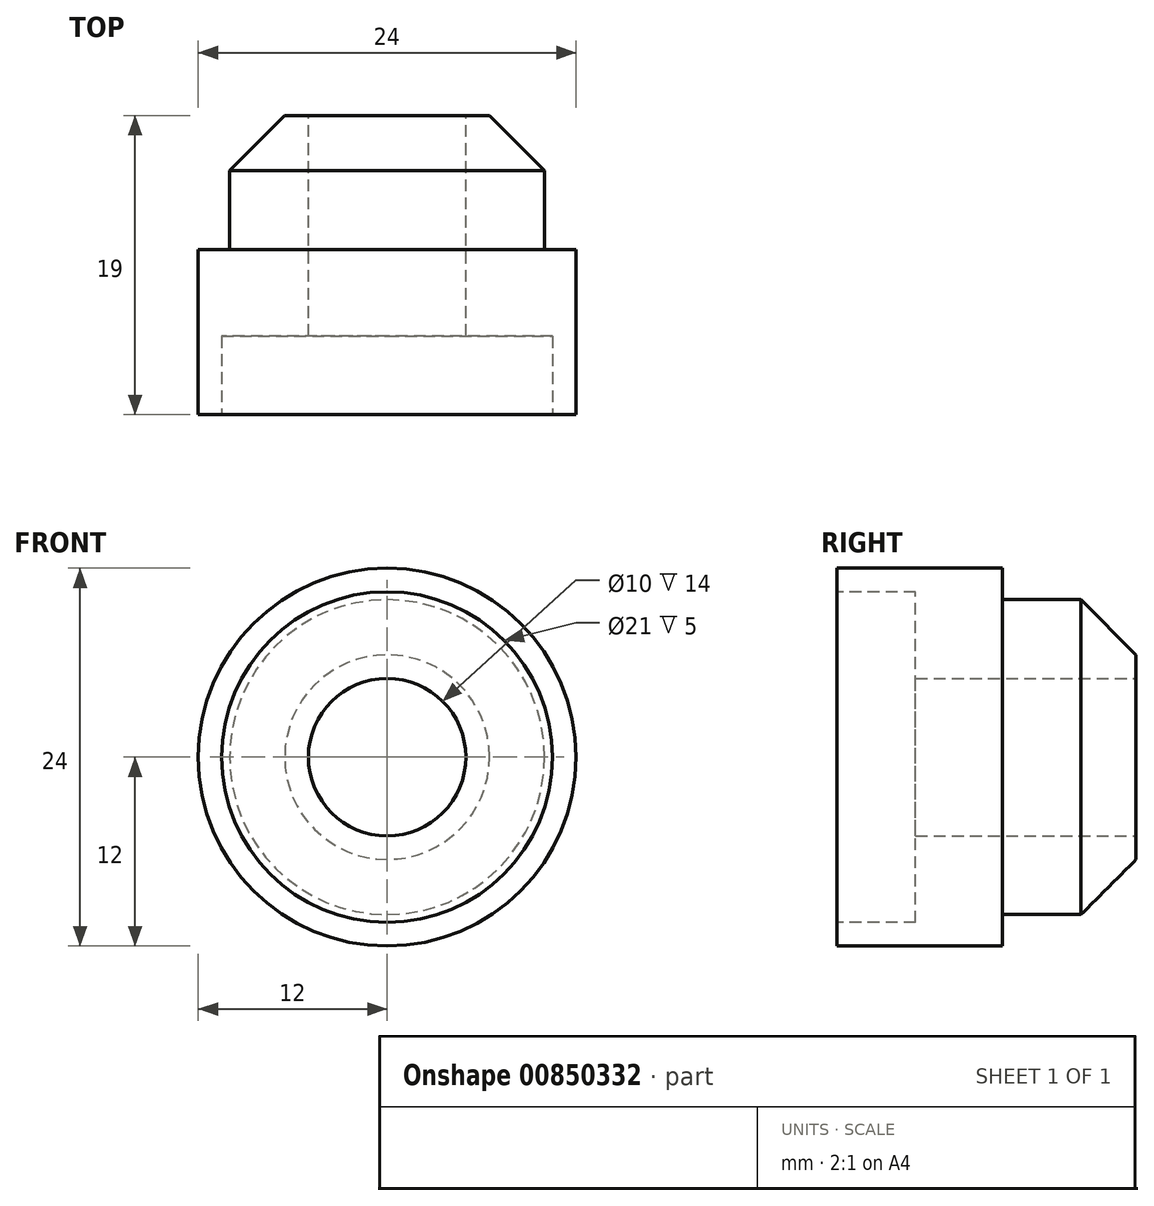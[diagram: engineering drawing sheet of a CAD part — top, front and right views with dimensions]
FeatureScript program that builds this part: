
annotation { "Feature Type Name" : "Feature", "Feature Type Description" : "" }
export const myFeature = defineFeature(function(context is Context, id is Id, definition is map)
    precondition{}
    {
        {
            var Q0;
            Q0=qCreatedBy(makeId("Front.planeOp"),FACE);
            var sketch = newSketch(context, id + "F0", { "sketchPlane" : qUnion([Q0])});
            skCircle(sketch, "E0", {"center": v(0, 0) * mm, "radius": 12 * mm});
            skSolve(sketch);
        }
        {
            var Q0;
            Q0 = qSketchRegion(id + "F0", true);
            extrude(context, id + "F1", {"entities" : qUnion([Q0]), "oppositeDirection" : true, "depth" : 19 * mm, "offsetDistance" : 25 * mm});
        }
        {
            var Q0;
            Q0=qCreatedBy(makeId("Front.planeOp"),FACE);
            cPlane(context, id + "F2", {"entities" : qUnion([Q0]), "cplaneType" : CPlaneType.OFFSET, "offset" : 10.5 * mm, "oppositeDirection" : true, "width" : 150 * mm, "height" : 150 * mm});
        }
        {
            var Q0;
            Q0=qCreatedBy(id+"F2.planeOp",FACE);
            var sketch = newSketch(context, id + "F3", { "sketchPlane" : qUnion([Q0])});
            skCircle(sketch, "E1", {"center": v(0, 0) * mm, "radius": 12 * mm});
            skCircle(sketch, "E2", {"center": v(0, 0) * mm, "radius": 10 * mm});
            skSolve(sketch);
        }
        {
            var Q0;
            Q0 = qSketchRegion(id + "F3", true);
            extrude(context, id + "F4", {"entities" : qUnion([Q0]), "operationType" : NewBodyOperationType.REMOVE, "oppositeDirection" : true, "depth" : 13 * mm, "offsetDistance" : 25 * mm});
        }
        {
            var Q0;
            Q0=makeQuery(id+"F1.opExtrude","CAP_FACE",FACE,{"disambiguationData":[OSD([sQuery(id+"F0.wireOp",EDGE,"E0")])],"isStart":false});
            cPlane(context, id + "F5", {"entities" : qUnion([Q0]), "cplaneType" : CPlaneType.OFFSET, "offset" : 0 * mm, "width" : 150 * mm, "height" : 150 * mm});
        }
        {
            var Q0;
            Q0=qCreatedBy(id+"F5.planeOp",FACE);
            var sketch = newSketch(context, id + "F6", { "sketchPlane" : qUnion([Q0])});
            skCircle(sketch, "E3", {"center": v(0, 0) * mm, "radius": 5 * mm});
            skSolve(sketch);
        }
        {
            var Q0;
            Q0=makeQuery(id+"F6.imprint","IMPRINT",FACE,{"disambiguationData":[TD([[makeQuery(id+"F6.imprint","IMPRINT",EDGE,{"derivedFrom":sQuery(id+"F6.wireOp",EDGE,"E3")}),1.0]])]});
            extrude(context, id + "F7", {"entities" : qUnion([Q0]), "operationType" : NewBodyOperationType.REMOVE, "oppositeDirection" : true, "depth" : 25 * mm, "offsetDistance" : 25 * mm});
        }
        {
            var Q0;
            Q0=qCreatedBy(makeId("Front.planeOp"),FACE);
            var sketch = newSketch(context, id + "F8", { "sketchPlane" : qUnion([Q0])});
            skCircle(sketch, "E4", {"center": v(0, 0) * mm, "radius": 12 * mm});
            skCircle(sketch, "E5", {"center": v(0, 0) * mm, "radius": 10.5 * mm});
            skSolve(sketch);
        }
        {
            var Q0;
            Q0=makeQuery(id+"F8.imprint","IMPRINT",FACE,{"disambiguationData":[TD([[makeQuery(id+"F8.imprint","IMPRINT",EDGE,{"derivedFrom":sQuery(id+"F8.wireOp",EDGE,"E5")}),1.0]])]});
            extrude(context, id + "F9", {"entities" : qUnion([Q0]), "operationType" : NewBodyOperationType.REMOVE, "oppositeDirection" : true, "depth" : 5 * mm, "offsetDistance" : 25 * mm});
        }
        {
            var Q0;
            Q0=makeQuery(id+"F4.boolean.opBoolean","INTERSECT",EDGE,{"derivedFrom":[makeQuery(id+"F1.opExtrude","CAP_FACE",FACE,{"disambiguationData":[OSD([sQuery(id+"F0.wireOp",EDGE,"E0")])],"isStart":false}),makeQuery(id+"F4.opExtrude","SWEPT_FACE",FACE,{"disambiguationData":[OSD([sQuery(id+"F3.wireOp",EDGE,"E2")])]})]});
            chamfer(context, id + "F10", {"entities" : qUnion([Q0]), "width" : 3.5 * mm, "tangentPropagation" : true});
        }
    });
